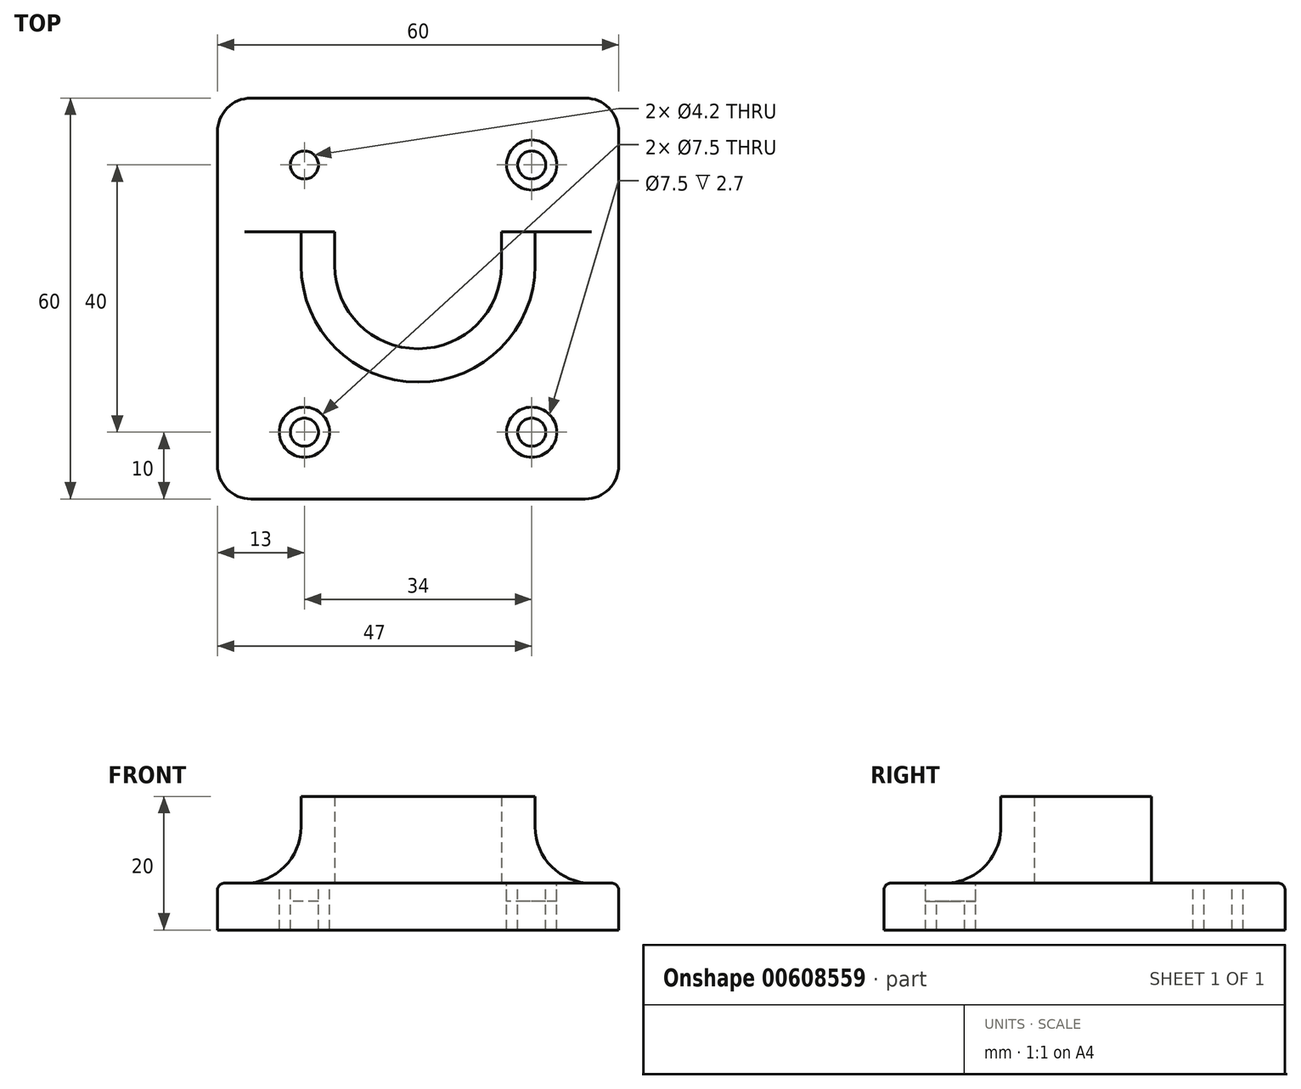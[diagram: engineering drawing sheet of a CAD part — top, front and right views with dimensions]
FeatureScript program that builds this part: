
annotation { "Feature Type Name" : "Feature", "Feature Type Description" : "" }
export const myFeature = defineFeature(function(context is Context, id is Id, definition is map)
    precondition{}
    {
        {
            var Q0;
            Q0=qCreatedBy(makeId("Top.planeOp"),FACE);
            var sketch = newSketch(context, id + "F0", { "sketchPlane" : qUnion([Q0])});
            skLineSegment(sketch, "E0.bottom", {"start": v(30, 30) * mm, "end": v(-30, 30) * mm});
            skLineSegment(sketch, "E0.top", {"start": v(30, -30) * mm, "end": v(-30, -30) * mm});
            skLineSegment(sketch, "E0.left", {"start": v(30, 30) * mm, "end": v(30, -30) * mm});
            skLineSegment(sketch, "E0.right", {"start": v(-30, 30) * mm, "end": v(-30, -30) * mm});
            skLineSegment(sketch, "E1", {"start": v(0, 0) * mm, "end": v(0, 5) * mm, "construction": true});
            skCircle(sketch, "E2", {"center": v(0, 5) * mm, "radius": 12.5 * mm});
            skCircle(sketch, "E3.0", {"center": v(0, 5) * mm, "radius": 17.5 * mm});
            skLineSegment(sketch, "E4", {"start": v(-17.5, 5) * mm, "end": v(-17.5, 10) * mm});
            skLineSegment(sketch, "E5", {"start": v(-17.5, 10) * mm, "end": v(-12.5, 10) * mm});
            skLineSegment(sketch, "E6", {"start": v(-12.5, 10) * mm, "end": v(-12.5, 5) * mm});
            skLineSegment(sketch, "E7.MirrorCS", {"start": v(17.5, 5) * mm, "end": v(17.5, 10) * mm});
            skLineSegment(sketch, "E8.MirrorCS", {"start": v(17.5, 10) * mm, "end": v(12.5, 10) * mm});
            skLineSegment(sketch, "E9.MirrorCS", {"start": v(12.5, 10) * mm, "end": v(12.5, 5) * mm});
            skSolve(sketch);
        }
        {
            var Q0;
            Q0=makeQuery(id+"F0.imprint","IMPRINT",FACE,{"disambiguationData":[TD([[makeQuery(id+"F0.imprint","IMPRINT",EDGE,{"derivedFrom":sQuery(id+"F0.wireOp",EDGE,"E0.bottom")}),1.0]])]});
            var Q1;
            {var subQ1=sQuery(id+"F0.wireOp",EDGE,"j0BzK7ga-Vi8E-Qmfq-ufuq-qfOxzBBBAaOd");Q1=makeQuery(id+"F0.imprint","IMPRINT",FACE,{"disambiguationData":[TD([[makeQuery(id+"F0.imprint","IMPRINT",EDGE,{"derivedFrom":subQ1}),-1.0]])]});}
            var Q2;
            {var subQ0=sQuery(id+"F0.wireOp",EDGE,"urMUrOSL-YJdR-bdW5-QNG1-7GoH4c0ts5vm");var subQ1=makeQuery(id+"F0.imprint","INTERSECT",VERTEX,{"derivedFrom":[subQ0,sQuery(id+"F0.wireOp",EDGE,"j0BzK7ga-Vi8E-Qmfq-ufuq-qfOxzBBBAaOd")]});Q2=makeQuery(id+"F0.imprint","IMPRINT",FACE,{"disambiguationData":[TD([[makeQuery(id+"F0.imprint","IMPRINT",EDGE,{"disambiguationData":[TD([[subQ1,1.0]])],"derivedFrom":subQ0}),1.0]])]});}
            var Q3;
            {var subQ8=sQuery(id+"F0.wireOp",EDGE,"j0BzK7ga-Vi8E-Qmfq-ufuq-qfOxzBBBAaOd");Q3=makeQuery(id+"F0.imprint","IMPRINT",FACE,{"disambiguationData":[TD([[makeQuery(id+"F0.imprint","IMPRINT",EDGE,{"derivedFrom":subQ8}),1.0]])]});}
            var Q4;
            {var subQ0=sQuery(id+"F0.wireOp",EDGE,"fcLtQy80-Fk5v-N7C7-KKXq-r9seXKgSIZUa");Q4=makeQuery(id+"F0.imprint","IMPRINT",FACE,{"disambiguationData":[TD([[makeQuery(id+"F0.imprint","IMPRINT",EDGE,{"derivedFrom":subQ0}),1.0]])]});}
            var Q5;
            {var subQ0=sQuery(id+"F0.wireOp",EDGE,"mEafH72T-v9uI-AiIg-Y6YW-eVlSJQao83Tz");Q5=makeQuery(id+"F0.imprint","IMPRINT",FACE,{"disambiguationData":[TD([[makeQuery(id+"F0.imprint","IMPRINT",EDGE,{"derivedFrom":subQ0}),-1.0]])]});}
            var Q6;
            {var subQ0=sQuery(id+"F0.wireOp",EDGE,"E2");var subQ1=makeQuery(id+"F0.imprint","INTERSECT",VERTEX,{"derivedFrom":[subQ0,sQuery(id+"F0.wireOp",EDGE,"E6")]});Q6=makeQuery(id+"F0.imprint","IMPRINT",FACE,{"disambiguationData":[TD([[makeQuery(id+"F0.imprint","IMPRINT",EDGE,{"disambiguationData":[TD([[subQ1,1.0]])],"derivedFrom":subQ0}),1.0]])]});}
            var Q7;
            {var subQ0=sQuery(id+"F0.wireOp",EDGE,"E6");Q7=makeQuery(id+"F0.imprint","IMPRINT",FACE,{"disambiguationData":[TD([[makeQuery(id+"F0.imprint","IMPRINT",EDGE,{"derivedFrom":subQ0}),1.0]])]});}
            var Q8;
            {var subQ8=sQuery(id+"F0.wireOp",EDGE,"E6");Q8=makeQuery(id+"F0.imprint","IMPRINT",FACE,{"disambiguationData":[TD([[makeQuery(id+"F0.imprint","IMPRINT",EDGE,{"derivedFrom":subQ8}),-1.0]])]});}
            var Q9;
            {var subQ0=sQuery(id+"F0.wireOp",EDGE,"E4");Q9=makeQuery(id+"F0.imprint","IMPRINT",FACE,{"disambiguationData":[TD([[makeQuery(id+"F0.imprint","IMPRINT",EDGE,{"derivedFrom":subQ0}),-1.0]])]});}
            var Q10;
            {var subQ0=sQuery(id+"F0.wireOp",EDGE,"E7.MirrorCS");Q10=makeQuery(id+"F0.imprint","IMPRINT",FACE,{"disambiguationData":[TD([[makeQuery(id+"F0.imprint","IMPRINT",EDGE,{"derivedFrom":subQ0}),1.0]])]});}
            extrude(context, id + "F1", {"entities" : qUnion([Q0, Q1, Q2, Q3, Q4, Q5, Q6, Q7, Q8, Q9, Q10]), "depth" : 7 * mm, "offsetDistance" : 25 * mm});
        }
        {
            var Q0;
            {var subQ8=sQuery(id+"F0.wireOp",EDGE,"E6");Q0=makeQuery(id+"F0.imprint","IMPRINT",FACE,{"disambiguationData":[TD([[makeQuery(id+"F0.imprint","IMPRINT",EDGE,{"derivedFrom":subQ8}),-1.0]])]});}
            var Q1;
            {var subQ0=sQuery(id+"F0.wireOp",EDGE,"E7.MirrorCS");Q1=makeQuery(id+"F0.imprint","IMPRINT",FACE,{"disambiguationData":[TD([[makeQuery(id+"F0.imprint","IMPRINT",EDGE,{"derivedFrom":subQ0}),1.0]])]});}
            var Q2;
            {var subQ0=sQuery(id+"F0.wireOp",EDGE,"E4");Q2=makeQuery(id+"F0.imprint","IMPRINT",FACE,{"disambiguationData":[TD([[makeQuery(id+"F0.imprint","IMPRINT",EDGE,{"derivedFrom":subQ0}),-1.0]])]});}
            extrude(context, id + "F2", {"entities" : qUnion([Q0, Q1, Q2]), "operationType" : NewBodyOperationType.ADD, "depth" : 20 * mm, "offsetDistance" : 25 * mm});
        }
        {
            var Q0;
            Q0=makeQuery(id+"F2.boolean.opBoolean","INTERSECT",EDGE,{"derivedFrom":[makeQuery(id+"F1.opExtrude","CAP_FACE",FACE,{"disambiguationData":[OSD([sQuery(id+"F0.wireOp",EDGE,"E0.bottom"),sQuery(id+"F0.wireOp",EDGE,"E0.top"),sQuery(id+"F0.wireOp",EDGE,"E0.left"),sQuery(id+"F0.wireOp",EDGE,"E0.right")])],"isStart":false}),makeQuery(id+"F2.opExtrude","SWEPT_FACE",FACE,{"disambiguationData":[OSD([sQuery(id+"F0.wireOp",EDGE,"E3.0")])]})]});
            var Q1;
            Q1=makeQuery(id+"F2.boolean.opBoolean","INTERSECT",EDGE,{"derivedFrom":[makeQuery(id+"F1.opExtrude","CAP_FACE",FACE,{"disambiguationData":[OSD([sQuery(id+"F0.wireOp",EDGE,"E0.bottom"),sQuery(id+"F0.wireOp",EDGE,"E0.top"),sQuery(id+"F0.wireOp",EDGE,"E0.left"),sQuery(id+"F0.wireOp",EDGE,"E0.right")])],"isStart":false}),makeQuery(id+"F2.opExtrude","SWEPT_FACE",FACE,{"disambiguationData":[OSD([sQuery(id+"F0.wireOp",EDGE,"E4")])]})]});
            var Q2;
            Q2=makeQuery(id+"F2.boolean.opBoolean","INTERSECT",EDGE,{"derivedFrom":[makeQuery(id+"F1.opExtrude","CAP_FACE",FACE,{"disambiguationData":[OSD([sQuery(id+"F0.wireOp",EDGE,"E0.bottom"),sQuery(id+"F0.wireOp",EDGE,"E0.top"),sQuery(id+"F0.wireOp",EDGE,"E0.left"),sQuery(id+"F0.wireOp",EDGE,"E0.right")])],"isStart":false}),makeQuery(id+"F2.opExtrude","SWEPT_FACE",FACE,{"disambiguationData":[OSD([sQuery(id+"F0.wireOp",EDGE,"E7.MirrorCS")])]})]});
            fillet(context, id + "F3", {"entities" : qUnion([Q0, Q1, Q2]), "radius" : 8.45 * mm, "tangentPropagation" : true, "allowEdgeOverflow" : false});
        }
        {
            var Q0;
            Q0=makeQuery(id+"F1.opExtrude","SWEPT_EDGE",EDGE,{"disambiguationData":[OSD([sQuery(id+"F0.wireOp",EDGE,"E0.top"),sQuery(id+"F0.wireOp",EDGE,"E0.left")])]});
            var Q1;
            Q1=makeQuery(id+"F1.opExtrude","SWEPT_EDGE",EDGE,{"disambiguationData":[OSD([sQuery(id+"F0.wireOp",EDGE,"E0.top"),sQuery(id+"F0.wireOp",EDGE,"E0.right")])]});
            var Q2;
            Q2=makeQuery(id+"F1.opExtrude","SWEPT_EDGE",EDGE,{"disambiguationData":[OSD([sQuery(id+"F0.wireOp",EDGE,"E0.bottom"),sQuery(id+"F0.wireOp",EDGE,"E0.right")])]});
            var Q3;
            Q3=makeQuery(id+"F1.opExtrude","SWEPT_EDGE",EDGE,{"disambiguationData":[OSD([sQuery(id+"F0.wireOp",EDGE,"E0.bottom"),sQuery(id+"F0.wireOp",EDGE,"E0.left")])]});
            fillet(context, id + "F4", {"entities" : qUnion([Q0, Q1, Q2, Q3]), "radius" : 5 * mm, "tangentPropagation" : true, "allowEdgeOverflow" : false});
        }
        {
            var Q0;
            Q0=makeQuery(id+"F1.opExtrude","CAP_EDGE",EDGE,{"disambiguationData":[OSD([sQuery(id+"F0.wireOp",EDGE,"E0.right")])],"isStart":false});
            var Q1;
            {var subQ0=sQuery(id+"F0.wireOp",EDGE,"E0.right");var subQ1=sQuery(id+"F0.wireOp",EDGE,"E0.bottom");Q1=makeQuery(id+"F4.opFillet","BLEND_EDGE",EDGE,{"blendedFrom":[makeQuery(id+"F1.opExtrude","SWEPT_EDGE",EDGE,{"disambiguationData":[OSD([subQ1,subQ0])]}),makeQuery(id+"F1.opExtrude","CAP_FACE",FACE,{"disambiguationData":[OSD([subQ1,sQuery(id+"F0.wireOp",EDGE,"E0.top"),sQuery(id+"F0.wireOp",EDGE,"E0.left"),subQ0])],"isStart":false})],"blendedInto":[makeQuery(id+"F1.opExtrude","CAP_FACE",FACE,{"disambiguationData":[OSD([subQ1,sQuery(id+"F0.wireOp",EDGE,"E0.top"),sQuery(id+"F0.wireOp",EDGE,"E0.left"),subQ0])],"isStart":false})]});}
            var Q2;
            Q2=makeQuery(id+"F1.opExtrude","CAP_EDGE",EDGE,{"disambiguationData":[OSD([sQuery(id+"F0.wireOp",EDGE,"E0.bottom")])],"isStart":false});
            var Q3;
            Q3=makeQuery(id+"F1.opExtrude","CAP_EDGE",EDGE,{"disambiguationData":[OSD([sQuery(id+"F0.wireOp",EDGE,"E0.left")])],"isStart":false});
            var Q4;
            {var subQ0=sQuery(id+"F0.wireOp",EDGE,"E0.left");var subQ1=sQuery(id+"F0.wireOp",EDGE,"E0.bottom");Q4=makeQuery(id+"F4.opFillet","BLEND_EDGE",EDGE,{"blendedFrom":[makeQuery(id+"F1.opExtrude","SWEPT_EDGE",EDGE,{"disambiguationData":[OSD([subQ1,subQ0])]}),makeQuery(id+"F1.opExtrude","CAP_FACE",FACE,{"disambiguationData":[OSD([subQ1,sQuery(id+"F0.wireOp",EDGE,"E0.top"),subQ0,sQuery(id+"F0.wireOp",EDGE,"E0.right")])],"isStart":false})],"blendedInto":[makeQuery(id+"F1.opExtrude","CAP_FACE",FACE,{"disambiguationData":[OSD([subQ1,sQuery(id+"F0.wireOp",EDGE,"E0.top"),subQ0,sQuery(id+"F0.wireOp",EDGE,"E0.right")])],"isStart":false})]});}
            var Q5;
            Q5=makeQuery(id+"F1.opExtrude","CAP_EDGE",EDGE,{"disambiguationData":[OSD([sQuery(id+"F0.wireOp",EDGE,"E0.top")])],"isStart":false});
            var Q6;
            {var subQ0=sQuery(id+"F0.wireOp",EDGE,"E0.right");var subQ1=sQuery(id+"F0.wireOp",EDGE,"E0.top");Q6=makeQuery(id+"F4.opFillet","BLEND_EDGE",EDGE,{"blendedFrom":[makeQuery(id+"F1.opExtrude","SWEPT_EDGE",EDGE,{"disambiguationData":[OSD([subQ1,subQ0])]}),makeQuery(id+"F1.opExtrude","CAP_FACE",FACE,{"disambiguationData":[OSD([sQuery(id+"F0.wireOp",EDGE,"E0.bottom"),subQ1,sQuery(id+"F0.wireOp",EDGE,"E0.left"),subQ0])],"isStart":false})],"blendedInto":[makeQuery(id+"F1.opExtrude","CAP_FACE",FACE,{"disambiguationData":[OSD([sQuery(id+"F0.wireOp",EDGE,"E0.bottom"),subQ1,sQuery(id+"F0.wireOp",EDGE,"E0.left"),subQ0])],"isStart":false})]});}
            var Q7;
            {var subQ0=sQuery(id+"F0.wireOp",EDGE,"E0.left");var subQ1=sQuery(id+"F0.wireOp",EDGE,"E0.top");Q7=makeQuery(id+"F4.opFillet","BLEND_EDGE",EDGE,{"blendedFrom":[makeQuery(id+"F1.opExtrude","SWEPT_EDGE",EDGE,{"disambiguationData":[OSD([subQ1,subQ0])]}),makeQuery(id+"F1.opExtrude","CAP_FACE",FACE,{"disambiguationData":[OSD([sQuery(id+"F0.wireOp",EDGE,"E0.bottom"),subQ1,subQ0,sQuery(id+"F0.wireOp",EDGE,"E0.right")])],"isStart":false})],"blendedInto":[makeQuery(id+"F1.opExtrude","CAP_FACE",FACE,{"disambiguationData":[OSD([sQuery(id+"F0.wireOp",EDGE,"E0.bottom"),subQ1,subQ0,sQuery(id+"F0.wireOp",EDGE,"E0.right")])],"isStart":false})]});}
            fillet(context, id + "F5", {"entities" : qUnion([Q0, Q1, Q2, Q3, Q4, Q5, Q6, Q7]), "radius" : 1 * mm, "tangentPropagation" : true, "allowEdgeOverflow" : false});
        }
        {
            var Q0;
            Q0=makeQuery(id+"F1.opExtrude","CAP_FACE",FACE,{"disambiguationData":[OSD([sQuery(id+"F0.wireOp",EDGE,"E0.bottom"),sQuery(id+"F0.wireOp",EDGE,"E0.top"),sQuery(id+"F0.wireOp",EDGE,"E0.left"),sQuery(id+"F0.wireOp",EDGE,"E0.right")])],"isStart":false});
            var sketch = newSketch(context, id + "F6", { "sketchPlane" : qUnion([Q0])});
            skLineSegment(sketch, "E10", {"start": v(0, 0) * mm, "end": v(0, 20) * mm, "construction": true});
            skLineSegment(sketch, "E11", {"start": v(0, 20) * mm, "end": v(17, 20) * mm, "construction": true});
            skLineSegment(sketch, "E12", {"start": v(0, 20) * mm, "end": v(-17, 20) * mm, "construction": true});
            skCircle(sketch, "E13", {"center": v(-17, 20) * mm, "radius": 3.75 * mm});
            skCircle(sketch, "E14", {"center": v(17, 20) * mm, "radius": 3.75 * mm});
            skLineSegment(sketch, "E15", {"start": v(0, 0) * mm, "end": v(0, 0) * mm});
            skLineSegment(sketch, "E16", {"start": v(0, 0) * mm, "end": v(0, -1.5) * mm, "construction": true});
            skLineSegment(sketch, "E17", {"start": v(0, -1.5) * mm, "end": v(-2.03, -1.5) * mm, "construction": true});
            skCircle(sketch, "E18", {"center": v(-17, 20) * mm, "radius": 2.1 * mm});
            skCircle(sketch, "E19.MirrorC", {"center": v(17, 20) * mm, "radius": 2.1 * mm});
            skCircle(sketch, "E20.MirrorC", {"center": v(-17, -20) * mm, "radius": 2.1 * mm});
            skCircle(sketch, "E21.MirrorC", {"center": v(17, -20) * mm, "radius": 2.1 * mm});
            skCircle(sketch, "E22.MirrorC", {"center": v(17, -20) * mm, "radius": 3.75 * mm});
            skCircle(sketch, "E23.MirrorC", {"center": v(-17, -20) * mm, "radius": 3.75 * mm});
            skSolve(sketch);
        }
        {
            var Q0;
            Q0=makeQuery(id+"F6.imprint","IMPRINT",FACE,{"disambiguationData":[TD([[makeQuery(id+"F6.imprint","IMPRINT",EDGE,{"derivedFrom":sQuery(id+"F6.wireOp",EDGE,"E18")}),1.0]])]});
            var Q1;
            Q1=makeQuery(id+"F6.imprint","IMPRINT",FACE,{"disambiguationData":[TD([[makeQuery(id+"F6.imprint","IMPRINT",EDGE,{"derivedFrom":sQuery(id+"F6.wireOp",EDGE,"E19.MirrorC")}),-1.0]])]});
            var Q2;
            Q2=makeQuery(id+"F6.imprint","IMPRINT",FACE,{"disambiguationData":[TD([[makeQuery(id+"F6.imprint","IMPRINT",EDGE,{"derivedFrom":sQuery(id+"F6.wireOp",EDGE,"7e420f3b-5e4f-46a2-b67e-972de88a384f0.MirrorC")}),1.0]])]});
            var Q3;
            Q3=makeQuery(id+"F6.imprint","IMPRINT",FACE,{"disambiguationData":[TD([[makeQuery(id+"F6.imprint","IMPRINT",EDGE,{"derivedFrom":sQuery(id+"F6.wireOp",EDGE,"6e3dbd85-6acb-47f0-9848-aa761cefcde80.MirrorC")}),-1.0]])]});
            var Q4;
            Q4=makeQuery(id+"F6.imprint","IMPRINT",FACE,{"disambiguationData":[TD([[makeQuery(id+"F6.imprint","IMPRINT",EDGE,{"derivedFrom":sQuery(id+"F6.wireOp",EDGE,"E20.MirrorC")}),-1.0]])]});
            var Q5;
            Q5=makeQuery(id+"F6.imprint","IMPRINT",FACE,{"disambiguationData":[TD([[makeQuery(id+"F6.imprint","IMPRINT",EDGE,{"derivedFrom":sQuery(id+"F6.wireOp",EDGE,"E21.MirrorC")}),1.0]])]});
            extrude(context, id + "F7", {"entities" : qUnion([Q0, Q1, Q2, Q3, Q4, Q5]), "operationType" : NewBodyOperationType.REMOVE, "oppositeDirection" : true, "depth" : 25 * mm, "offsetDistance" : 25 * mm});
        }
        {
            var Q0;
            Q0=makeQuery(id+"F6.imprint","IMPRINT",FACE,{"disambiguationData":[TD([[makeQuery(id+"F6.imprint","IMPRINT",EDGE,{"derivedFrom":sQuery(id+"F6.wireOp",EDGE,"E13")}),-1.0]])]});
            var Q1;
            Q1=makeQuery(id+"F6.imprint","IMPRINT",FACE,{"disambiguationData":[TD([[makeQuery(id+"F6.imprint","IMPRINT",EDGE,{"derivedFrom":sQuery(id+"F6.wireOp",EDGE,"E14")}),-1.0]])]});
            var Q2;
            Q2=makeQuery(id+"F6.imprint","IMPRINT",FACE,{"disambiguationData":[TD([[makeQuery(id+"F6.imprint","IMPRINT",EDGE,{"derivedFrom":sQuery(id+"F6.wireOp",EDGE,"89b5405d-507c-4acf-8d33-0d0273979da60.MirrorC")}),1.0]])]});
            var Q3;
            Q3=makeQuery(id+"F6.imprint","IMPRINT",FACE,{"disambiguationData":[TD([[makeQuery(id+"F6.imprint","IMPRINT",EDGE,{"derivedFrom":sQuery(id+"F6.wireOp",EDGE,"c7313028-236e-457b-97ca-b10f8dcce06e0.MirrorC")}),1.0]])]});
            var Q4;
            Q4=makeQuery(id+"F6.imprint","IMPRINT",FACE,{"disambiguationData":[TD([[makeQuery(id+"F6.imprint","IMPRINT",EDGE,{"derivedFrom":sQuery(id+"F6.wireOp",EDGE,"E20.MirrorC")}),1.0]])]});
            var Q5;
            Q5=makeQuery(id+"F6.imprint","IMPRINT",FACE,{"disambiguationData":[TD([[makeQuery(id+"F6.imprint","IMPRINT",EDGE,{"derivedFrom":sQuery(id+"F6.wireOp",EDGE,"E21.MirrorC")}),-1.0]])]});
            extrude(context, id + "F8", {"entities" : qUnion([Q0, Q1, Q2, Q3, Q4, Q5]), "operationType" : NewBodyOperationType.REMOVE, "oppositeDirection" : true, "depth" : 2.7 * mm, "offsetDistance" : 25 * mm});
        }
    });
